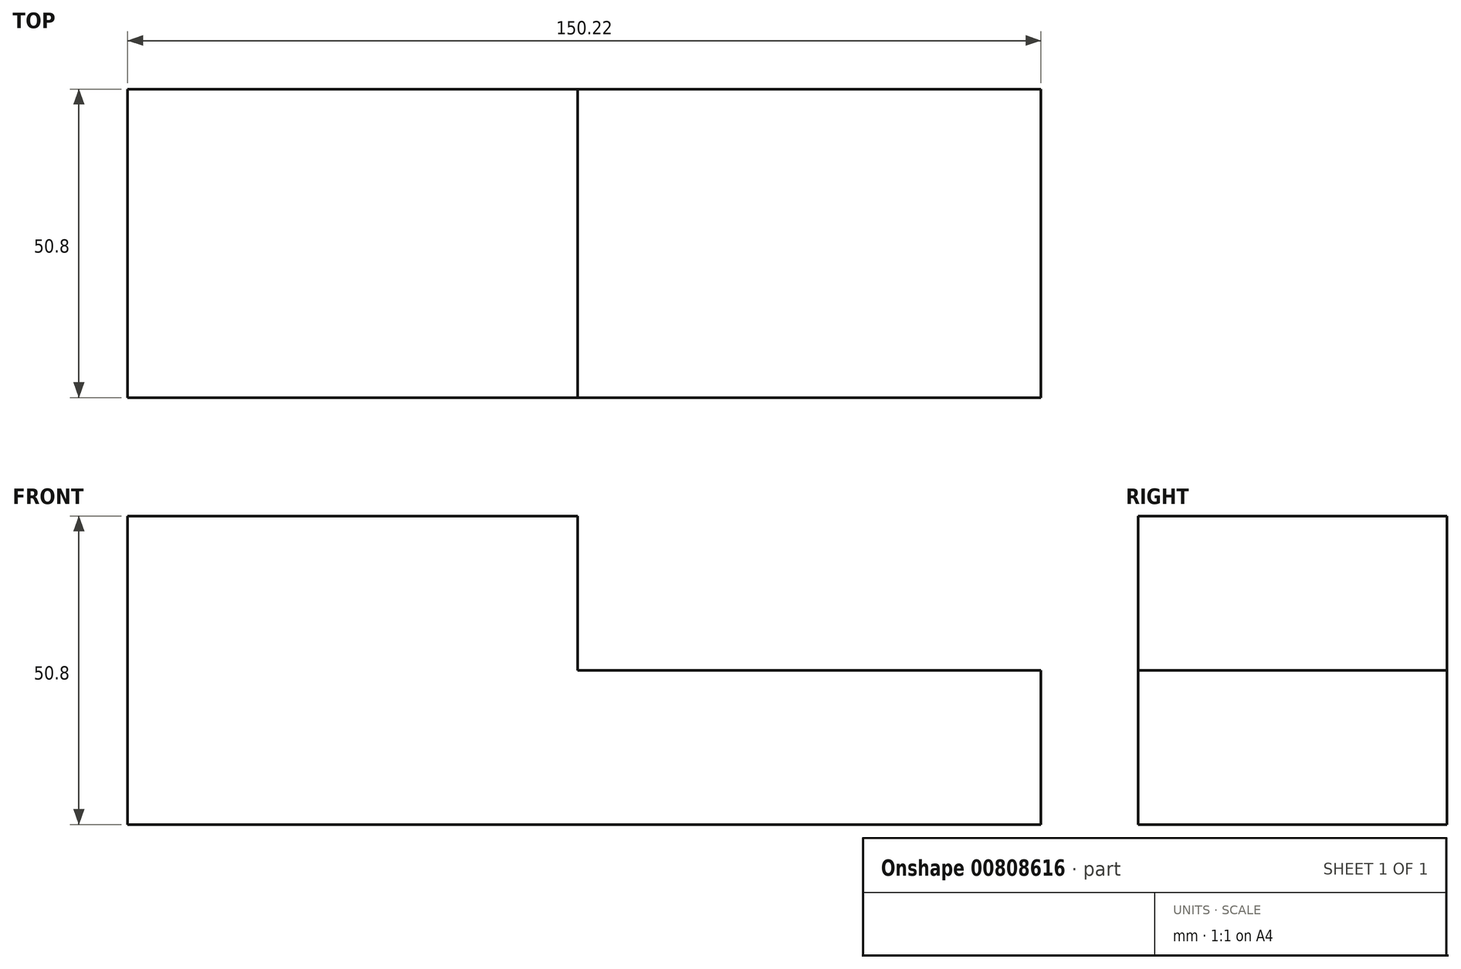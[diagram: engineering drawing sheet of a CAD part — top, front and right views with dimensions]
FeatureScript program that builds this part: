
annotation { "Feature Type Name" : "Feature", "Feature Type Description" : "" }
export const myFeature = defineFeature(function(context is Context, id is Id, definition is map)
    precondition{}
    {
        {
            var Q0;
            Q0=qCreatedBy(makeId("Front.planeOp"),FACE);
            var sketch = newSketch(context, id + "F0", { "sketchPlane" : qUnion([Q0])});
            skLineSegment(sketch, "E0", {"start": v(-76.26, 0) * mm, "end": v(-76.26, 50.8) * mm});
            skLineSegment(sketch, "E1", {"start": v(-78.44, 0) * mm, "end": v(73.96, 0) * mm});
            skLineSegment(sketch, "E2", {"start": v(73.96, 0) * mm, "end": v(73.96, 25.4) * mm});
            skLineSegment(sketch, "E3", {"start": v(73.96, 25.4) * mm, "end": v(-2.24, 25.4) * mm});
            skLineSegment(sketch, "E4", {"start": v(-2.24, 25.4) * mm, "end": v(-2.24, 50.8) * mm});
            skLineSegment(sketch, "E5", {"start": v(-2.24, 50.8) * mm, "end": v(-76.26, 50.8) * mm});
            skSolve(sketch);
        }
        {
            var Q0;
            {var subQ2=sQuery(id+"F0.wireOp",EDGE,"E0");Q0=makeQuery(id+"F0.imprint","IMPRINT",FACE,{"disambiguationData":[TD([[makeQuery(id+"F0.imprint","IMPRINT",EDGE,{"derivedFrom":subQ2}),-1.0]])]});}
            extrude(context, id + "F1", {"entities" : qUnion([Q0]), "depth" : 50.8 * mm, "offsetDistance" : 25.4 * mm});
        }
    });
